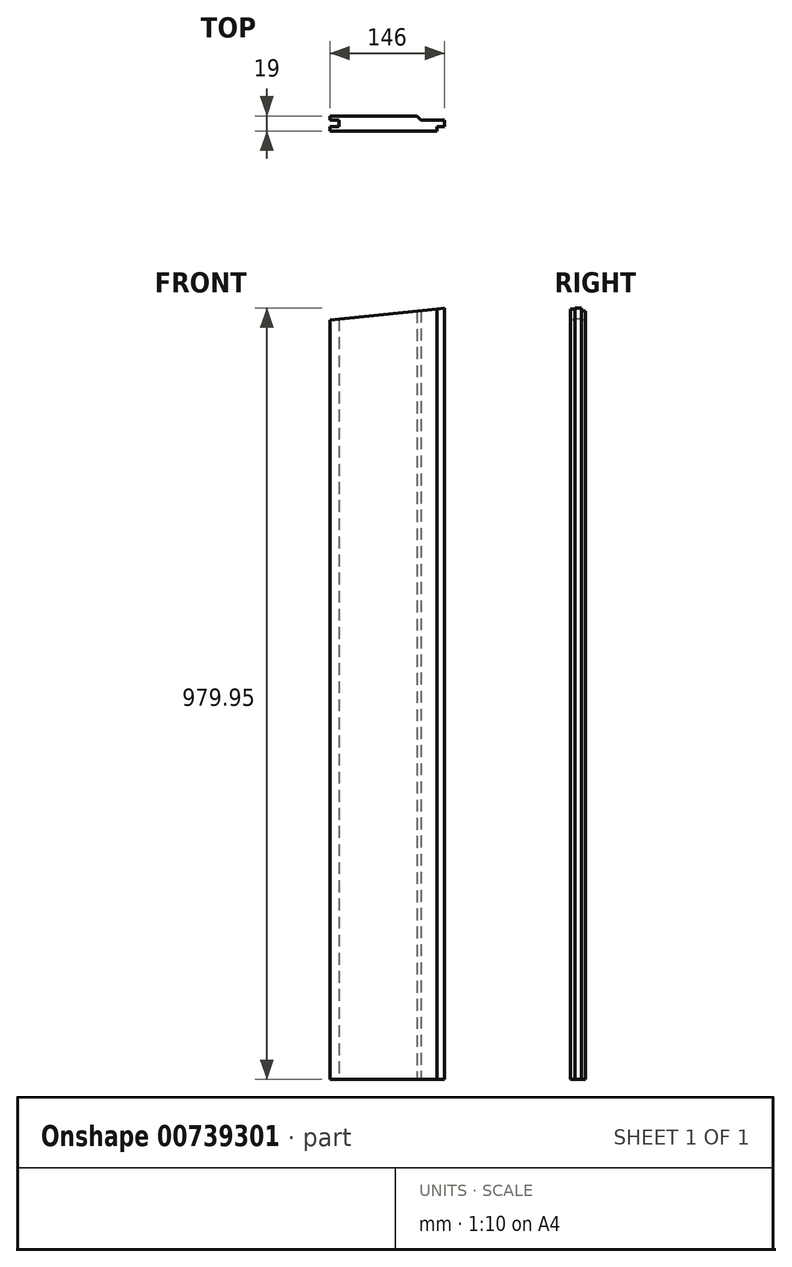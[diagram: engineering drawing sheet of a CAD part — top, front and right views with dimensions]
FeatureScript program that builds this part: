
annotation { "Feature Type Name" : "Feature", "Feature Type Description" : "" }
export const myFeature = defineFeature(function(context is Context, id is Id, definition is map)
    precondition{}
    {
        {
            var Q0;
            Q0=qCreatedBy(makeId("Top.planeOp"),FACE);
            var sketch = newSketch(context, id + "F0", { "sketchPlane" : qUnion([Q0])});
            skLineSegment(sketch, "E0.bottom", {"start": v(0, -9.5) * mm, "end": v(136, -9.5) * mm});
            skLineSegment(sketch, "E0.top", {"start": v(0, 9.5) * mm, "end": v(110.5, 9.5) * mm});
            skLineSegment(sketch, "E0.left", {"start": v(0, -9.5) * mm, "end": v(0, -4) * mm});
            skLineSegment(sketch, "E0.right", {"start": v(136, -9.5) * mm, "end": v(136, -4) * mm});
            skLineSegment(sketch, "E1", {"start": v(0, -4) * mm, "end": v(12, -4) * mm});
            skLineSegment(sketch, "E2", {"start": v(12, -4) * mm, "end": v(12, 4) * mm});
            skLineSegment(sketch, "E3", {"start": v(12, 4) * mm, "end": v(0, 4) * mm});
            skLineSegment(sketch, "E4.trimOffspring", {"start": v(0, 4) * mm, "end": v(0, 9.5) * mm});
            skLineSegment(sketch, "E5", {"start": v(136, -4) * mm, "end": v(146, -4) * mm});
            skLineSegment(sketch, "E6", {"start": v(146, -4) * mm, "end": v(146, 4) * mm});
            skLineSegment(sketch, "E7", {"start": v(146, 4) * mm, "end": v(116, 4) * mm});
            skLineSegment(sketch, "E8.trimOffspring", {"start": v(116, 4) * mm, "end": v(110.5, 9.5) * mm});
            skSolve(sketch);
        }
        {
            var Q0;
            Q0=makeQuery(id+"F0.imprint","IMPRINT",FACE,{"disambiguationData":[TD([[makeQuery(id+"F0.imprint","IMPRINT",EDGE,{"derivedFrom":sQuery(id+"F0.wireOp",EDGE,"E0.bottom")}),1.0]])]});
            extrude(context, id + "F1", {"entities" : qUnion([Q0]), "depth" : 1100 * mm, "offsetDistance" : 25 * mm});
        }
        {
            var Q0;
            Q0=makeQuery(id+"F1.opExtrude","SWEPT_FACE",FACE,{"disambiguationData":[OSD([sQuery(id+"F0.wireOp",EDGE,"E0.top")])]});
            var sketch = newSketch(context, id + "F2", { "sketchPlane" : qUnion([Q0])});
            skLineSegment(sketch, "E9", {"start": v(-1288.15, 1100) * mm, "end": v(139, 950) * mm});
            skLineSegment(sketch, "E10", {"start": v(139, 950) * mm, "end": v(139, 1100) * mm});
            skLineSegment(sketch, "E11", {"start": v(139, 1100) * mm, "end": v(-1288.15, 1100) * mm});
            skSolve(sketch);
        }
        {
            var Q0;
            {var subQ0=sQuery(id+"F2.wireOp",EDGE,"E11");var subQ1=sQuery(id+"F2.wireOp",EDGE,"E9");var subQ2=makeQuery(id+"F2.imprint","INTERSECT",VERTEX,{"derivedFrom":[subQ1,subQ0]});Q0=makeQuery(id+"F2.imprint","IMPRINT",FACE,{"disambiguationData":[TD([[makeQuery(id+"F2.imprint","IMPRINT",EDGE,{"disambiguationData":[TD([[subQ2,-1.0]])],"derivedFrom":subQ1}),1.0]])]});}
            var Q1;
            {var subQ0=sQuery(id+"F2.wireOp",EDGE,"E10");Q1=makeQuery(id+"F2.imprint","IMPRINT",FACE,{"disambiguationData":[TD([[makeQuery(id+"F2.imprint","IMPRINT",EDGE,{"derivedFrom":subQ0}),1.0]])]});}
            var Q2;
            {var subQ0=sQuery(id+"F2.wireOp",EDGE,"E9");var subQ1=sQuery(id+"F0.wireOp",EDGE,"E0.top");var subQ2=makeQuery(id+"F1.opExtrude","SWEPT_EDGE",EDGE,{"disambiguationData":[OSD([subQ1,sQuery(id+"F0.wireOp",EDGE,"E8.trimOffspring")])]});var subQ3=makeQuery(id+"F2.imprint","INTERSECT",VERTEX,{"derivedFrom":[subQ2,subQ0]});Q2=makeQuery(id+"F2.imprint","IMPRINT",FACE,{"disambiguationData":[TD([[makeQuery(id+"F2.imprint","IMPRINT",EDGE,{"disambiguationData":[TD([[subQ3,-1.0]])],"derivedFrom":subQ0}),1.0]])]});}
            extrude(context, id + "F3", {"entities" : qUnion([Q0, Q1, Q2]), "operationType" : NewBodyOperationType.REMOVE, "endBound" : BoundingType.THROUGH_ALL, "oppositeDirection" : true, "depth" : 25 * mm, "offsetDistance" : 25 * mm});
        }
    });
